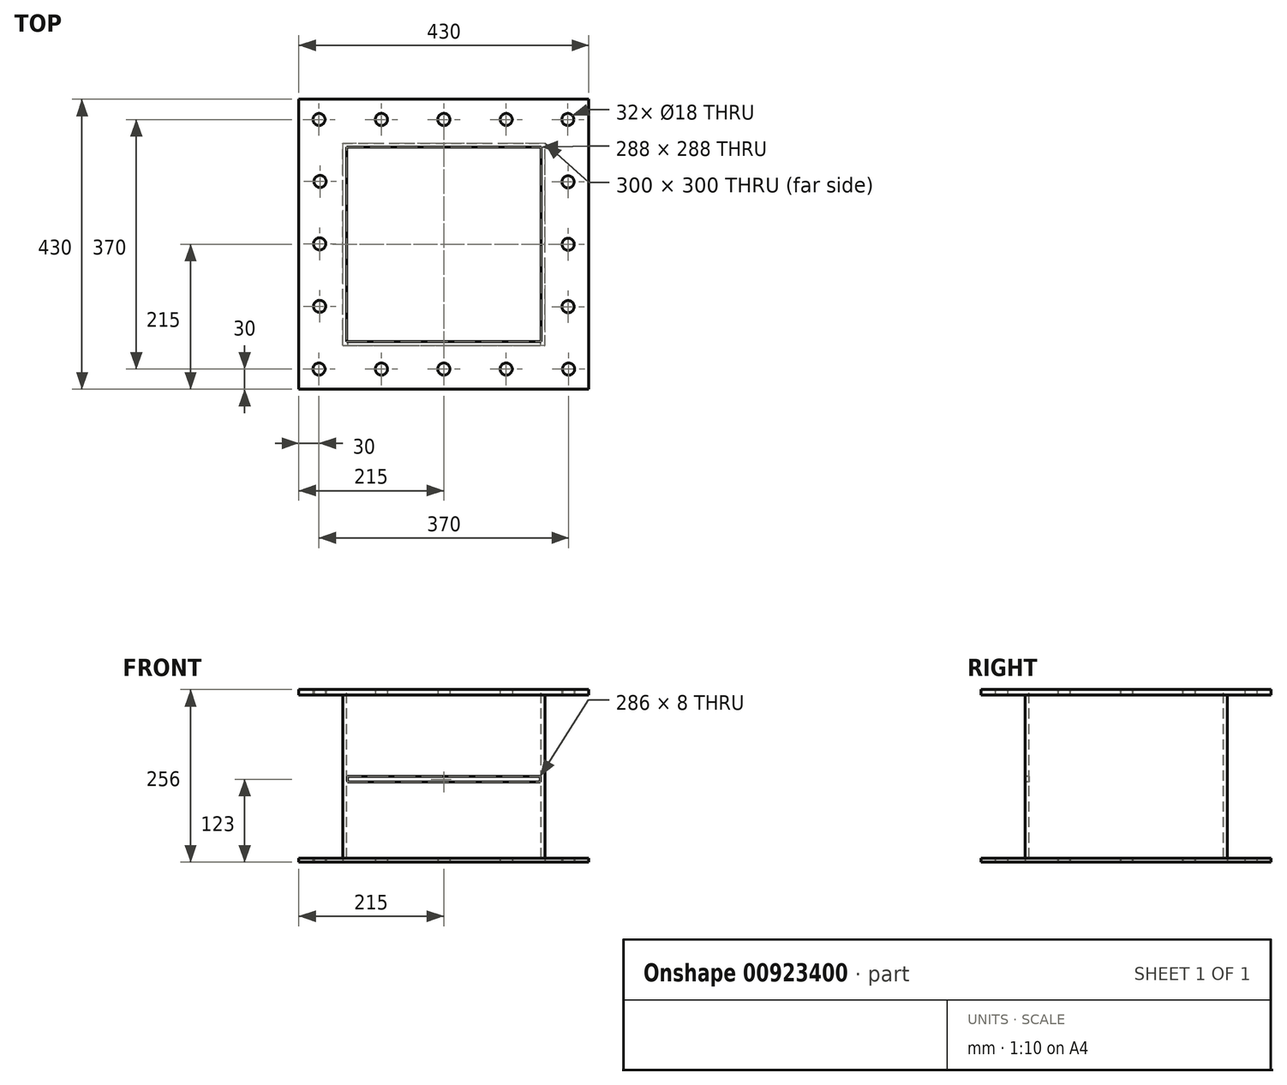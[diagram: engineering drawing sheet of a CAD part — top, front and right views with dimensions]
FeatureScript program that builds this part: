
annotation { "Feature Type Name" : "Feature", "Feature Type Description" : "" }
export const myFeature = defineFeature(function(context is Context, id is Id, definition is map)
    precondition{}
    {
        {
            var Q0;
            Q0=qCreatedBy(makeId("Top.planeOp"),FACE);
            var sketch = newSketch(context, id + "F0", { "sketchPlane" : qUnion([Q0])});
            skLineSegment(sketch, "E0.bottom", {"start": v(-215.44, -118.11) * mm, "end": v(214.56, -118.11) * mm});
            skLineSegment(sketch, "E0.top", {"start": v(-215.44, 311.89) * mm, "end": v(214.56, 311.89) * mm});
            skLineSegment(sketch, "E0.left", {"start": v(-215.44, -118.11) * mm, "end": v(-215.44, 311.89) * mm});
            skLineSegment(sketch, "E0.right", {"start": v(214.56, -118.11) * mm, "end": v(214.56, 311.89) * mm});
            skLineSegment(sketch, "E1.0", {"start": v(-150.44, -53.11) * mm, "end": v(149.56, -53.11) * mm});
            skLineSegment(sketch, "E1.1", {"start": v(-150.44, -53.11) * mm, "end": v(-150.44, 246.89) * mm});
            skLineSegment(sketch, "E1.2", {"start": v(-150.44, 246.89) * mm, "end": v(149.56, 246.89) * mm});
            skLineSegment(sketch, "E1.3", {"start": v(149.56, -53.11) * mm, "end": v(149.56, 246.89) * mm});
            skSolve(sketch);
        }
        {
            var Q0;
            Q0=makeQuery(id+"F0.imprint","IMPRINT",FACE,{"disambiguationData":[TD([[makeQuery(id+"F0.imprint","IMPRINT",EDGE,{"derivedFrom":sQuery(id+"F0.wireOp",EDGE,"E0.bottom")}),1.0]])]});
            extrude(context, id + "F1", {"entities" : qUnion([Q0]), "depth" : 6 * mm, "offsetDistance" : 25.4 * mm});
        }
        {
            var Q0;
            Q0=makeQuery(id+"F1.opExtrude","CAP_FACE",FACE,{"disambiguationData":[OSD([sQuery(id+"F0.wireOp",EDGE,"E0.bottom"),sQuery(id+"F0.wireOp",EDGE,"E0.top"),sQuery(id+"F0.wireOp",EDGE,"E0.left"),sQuery(id+"F0.wireOp",EDGE,"E0.right"),sQuery(id+"F0.wireOp",EDGE,"E1.0"),sQuery(id+"F0.wireOp",EDGE,"E1.1"),sQuery(id+"F0.wireOp",EDGE,"E1.2"),sQuery(id+"F0.wireOp",EDGE,"E1.3")])],"isStart":false});
            var sketch = newSketch(context, id + "F2", { "sketchPlane" : qUnion([Q0])});
            skLineSegment(sketch, "E2.0", {"start": v(-150.44, -53.11) * mm, "end": v(-150.44, 246.89) * mm});
            skLineSegment(sketch, "E3.0", {"start": v(-150.44, 246.89) * mm, "end": v(149.56, 246.89) * mm});
            skLineSegment(sketch, "E4.0", {"start": v(149.56, -53.11) * mm, "end": v(149.56, 246.89) * mm});
            skLineSegment(sketch, "E5.0", {"start": v(-150.44, -53.11) * mm, "end": v(149.56, -53.11) * mm});
            skSolve(sketch);
        }
        {
            var Q0;
            Q0=makeQuery(id+"F2.imprint","IMPRINT",FACE,{"disambiguationData":[TD([[makeQuery(id+"F2.imprint","IMPRINT",EDGE,{"derivedFrom":sQuery(id+"F2.wireOp",EDGE,"E5.0")}),1.0]])]});
            extrude(context, id + "F3", {"entities" : qUnion([Q0]), "depth" : 250 * mm, "offsetDistance" : 25.4 * mm});
        }
        {
            var Q0;
            Q0=makeQuery(id+"F3.opExtrude","CAP_FACE",FACE,{"disambiguationData":[OSD([sQuery(id+"F2.wireOp",EDGE,"E5.0"),sQuery(id+"F2.wireOp",EDGE,"E3.0"),sQuery(id+"F2.wireOp",EDGE,"E2.0"),sQuery(id+"F2.wireOp",EDGE,"E4.0")])],"isStart":false});
            var sketch = newSketch(context, id + "F4", { "sketchPlane" : qUnion([Q0])});
            skLineSegment(sketch, "E6.0", {"start": v(143.56, -47.11) * mm, "end": v(143.56, 240.89) * mm});
            skLineSegment(sketch, "E6.1", {"start": v(-144.44, -47.11) * mm, "end": v(143.56, -47.11) * mm});
            skLineSegment(sketch, "E6.2", {"start": v(-144.44, -47.11) * mm, "end": v(-144.44, 240.89) * mm});
            skLineSegment(sketch, "E6.3", {"start": v(-144.44, 240.89) * mm, "end": v(143.56, 240.89) * mm});
            skSolve(sketch);
        }
        {
            var Q0;
            Q0=makeQuery(id+"F4.imprint","IMPRINT",FACE,{"disambiguationData":[TD([[makeQuery(id+"F4.imprint","IMPRINT",EDGE,{"derivedFrom":sQuery(id+"F4.wireOp",EDGE,"E6.0")}),1.0]])]});
            extrude(context, id + "F5", {"entities" : qUnion([Q0]), "operationType" : NewBodyOperationType.REMOVE, "oppositeDirection" : true, "depth" : 566.42 * mm, "offsetDistance" : 25.4 * mm});
        }
        {
            var Q0;
            Q0=makeQuery(id+"F3.opExtrude","CAP_FACE",FACE,{"disambiguationData":[OSD([sQuery(id+"F2.wireOp",EDGE,"E5.0"),sQuery(id+"F2.wireOp",EDGE,"E3.0"),sQuery(id+"F2.wireOp",EDGE,"E2.0"),sQuery(id+"F2.wireOp",EDGE,"E4.0")])],"isStart":false});
            var sketch = newSketch(context, id + "F6", { "sketchPlane" : qUnion([Q0])});
            skLineSegment(sketch, "E7.bottom", {"start": v(-150.44, 246.89) * mm, "end": v(149.56, 246.89) * mm});
            skLineSegment(sketch, "E7.top", {"start": v(-150.44, -53.11) * mm, "end": v(149.56, -53.11) * mm});
            skLineSegment(sketch, "E7.left", {"start": v(-150.44, 246.89) * mm, "end": v(-150.44, -53.11) * mm});
            skLineSegment(sketch, "E7.right", {"start": v(149.56, 246.89) * mm, "end": v(149.56, -53.11) * mm});
            skLineSegment(sketch, "E8.0", {"start": v(214.56, 311.89) * mm, "end": v(214.56, -118.11) * mm});
            skLineSegment(sketch, "E8.1", {"start": v(-215.44, 311.89) * mm, "end": v(214.56, 311.89) * mm});
            skLineSegment(sketch, "E8.2", {"start": v(-215.44, 311.89) * mm, "end": v(-215.44, -118.11) * mm});
            skLineSegment(sketch, "E8.3", {"start": v(-215.44, -118.11) * mm, "end": v(214.56, -118.11) * mm});
            skSolve(sketch);
        }
        {
            var Q0;
            Q0=makeQuery(id+"F6.imprint","IMPRINT",FACE,{"disambiguationData":[TD([[makeQuery(id+"F6.imprint","IMPRINT",EDGE,{"derivedFrom":sQuery(id+"F6.wireOp",EDGE,"E7.bottom")}),1.0]])]});
            extrude(context, id + "F7", {"entities" : qUnion([Q0]), "operationType" : NewBodyOperationType.ADD, "oppositeDirection" : true, "depth" : 8 * mm, "offsetDistance" : 25.4 * mm});
        }
        {
            var Q0;
            Q0=makeQuery(id+"F3.opExtrude","SWEPT_FACE",FACE,{"disambiguationData":[OSD([sQuery(id+"F2.wireOp",EDGE,"E5.0")])]});
            var sketch = newSketch(context, id + "F8", { "sketchPlane" : qUnion([Q0])});
            skLineSegment(sketch, "E9.0", {"start": v(-143.44, 127) * mm, "end": v(-143.44, 119) * mm});
            skLineSegment(sketch, "E10.0", {"start": v(142.56, 127) * mm, "end": v(142.56, 119) * mm});
            skLineSegment(sketch, "E11", {"start": v(-143.44, 127) * mm, "end": v(142.56, 127) * mm});
            skLineSegment(sketch, "E12.0", {"start": v(-143.44, 119) * mm, "end": v(142.56, 119) * mm});
            skPoint(sketch, "E13.orphan", {"position": v(-143.44, 248) * mm});
            skPoint(sketch, "E14.orphan", {"position": v(-143.44, 6) * mm});
            skPoint(sketch, "E15.orphan", {"position": v(142.56, 6) * mm});
            skPoint(sketch, "E16.orphan", {"position": v(142.56, 248) * mm});
            skSolve(sketch);
        }
        {
            var Q0;
            Q0=makeQuery(id+"F8.imprint","IMPRINT",FACE,{"disambiguationData":[TD([[makeQuery(id+"F8.imprint","IMPRINT",EDGE,{"derivedFrom":sQuery(id+"F8.wireOp",EDGE,"E9.0")}),1.0]])]});
            var Q1;
            Q1=makeQuery(id+"F5.boolean.opBoolean","COPY",FACE,{"derivedFrom":makeQuery(id+"F5.opExtrude","SWEPT_FACE",FACE,{"disambiguationData":[OSD([sQuery(id+"F4.wireOp",EDGE,"E6.3")])]})});
            extrude(context, id + "F9", {"entities" : qUnion([Q0]), "operationType" : NewBodyOperationType.REMOVE, "endBound" : BoundingType.UP_TO_SURFACE, "oppositeDirection" : true, "depth" : 279.4 * mm, "endBoundEntityFace" : qUnion([Q1]), "offsetDistance" : 25.4 * mm});
        }
        {
            var Q0;
            Q0=makeQuery(id+"F7.boolean.opBoolean","MERGE",FACE,{"derivedFrom":[makeQuery(id+"F3.opExtrude","CAP_FACE",FACE,{"disambiguationData":[OSD([sQuery(id+"F2.wireOp",EDGE,"E5.0"),sQuery(id+"F2.wireOp",EDGE,"E3.0"),sQuery(id+"F2.wireOp",EDGE,"E2.0"),sQuery(id+"F2.wireOp",EDGE,"E4.0")])],"isStart":false}),makeQuery(id+"F7.opExtrude","CAP_FACE",FACE,{"disambiguationData":[OSD([sQuery(id+"F6.wireOp",EDGE,"E7.bottom"),sQuery(id+"F6.wireOp",EDGE,"E7.top"),sQuery(id+"F6.wireOp",EDGE,"E7.left"),sQuery(id+"F6.wireOp",EDGE,"E7.right"),sQuery(id+"F6.wireOp",EDGE,"E8.0"),sQuery(id+"F6.wireOp",EDGE,"E8.1"),sQuery(id+"F6.wireOp",EDGE,"E8.2"),sQuery(id+"F6.wireOp",EDGE,"E8.3")])],"isStart":true})]});
            var sketch = newSketch(context, id + "F10", { "sketchPlane" : qUnion([Q0])});
            skCircle(sketch, "E17", {"center": v(184.56, -88.11) * mm, "radius": 9 * mm});
            skCircle(sketch, "E18.1.0.0", {"center": v(92.06, -88.11) * mm, "radius": 9 * mm});
            skCircle(sketch, "E18.2.0.0", {"center": v(-0.44, -88.11) * mm, "radius": 9 * mm});
            skCircle(sketch, "E18.3.0.0", {"center": v(-92.94, -88.11) * mm, "radius": 9 * mm});
            skCircle(sketch, "E18.4.0.0", {"center": v(-185.44, -88.11) * mm, "radius": 9 * mm});
            skLineSegment(sketch, "E18.direction1", {"start": v(184.56, -88.11) * mm, "end": v(92.06, -88.11) * mm, "construction": true});
            skCircle(sketch, "E19.MirrorC", {"center": v(-185.44, 281.89) * mm, "radius": 9 * mm});
            skCircle(sketch, "E20.MirrorC", {"center": v(-92.94, 281.89) * mm, "radius": 9 * mm});
            skCircle(sketch, "E21.MirrorC", {"center": v(-0.44, 281.89) * mm, "radius": 9 * mm});
            skCircle(sketch, "E22.MirrorC", {"center": v(92.06, 281.89) * mm, "radius": 9 * mm});
            skCircle(sketch, "E23.MirrorC", {"center": v(183.48, 281.89) * mm, "radius": 9 * mm});
            skLineSegment(sketch, "E24", {"start": v(184.56, -88.11) * mm, "end": v(184.54, -79.11) * mm});
            skCircle(sketch, "E25", {"center": v(184.02, 96.89) * mm, "radius": 9 * mm});
            skCircle(sketch, "E26", {"center": v(183.75, 189.39) * mm, "radius": 9 * mm});
            skCircle(sketch, "E27.MirrorC", {"center": v(183.75, 4.4) * mm, "radius": 9 * mm});
            skCircle(sketch, "E28.MirrorC", {"center": v(-184.47, 4.95) * mm, "radius": 9 * mm});
            skCircle(sketch, "E29.MirrorC", {"center": v(-183.9, 189.95) * mm, "radius": 9 * mm});
            skCircle(sketch, "E30.MirrorC", {"center": v(-184.46, 97.45) * mm, "radius": 9 * mm});
            skSolve(sketch);
        }
        {
            var Q0;
            Q0=sQuery(id+"F10.wireOp",VERTEX,"E18.4.0.0.center");
            var Q1;
            Q1=sQuery(id+"F10.wireOp",VERTEX,"E28.MirrorC.center");
            var Q2;
            Q2=sQuery(id+"F10.wireOp",VERTEX,"E30.MirrorC.center");
            var Q3;
            Q3=sQuery(id+"F10.wireOp",VERTEX,"E29.MirrorC.center");
            var Q4;
            Q4=sQuery(id+"F10.wireOp",VERTEX,"E19.MirrorC.center");
            var Q5;
            Q5=sQuery(id+"F10.wireOp",VERTEX,"E20.MirrorC.center");
            var Q6;
            Q6=sQuery(id+"F10.wireOp",VERTEX,"E21.MirrorC.center");
            var Q7;
            Q7=sQuery(id+"F10.wireOp",VERTEX,"E22.MirrorC.center");
            var Q8;
            Q8=sQuery(id+"F10.wireOp",VERTEX,"E23.MirrorC.center");
            var Q9;
            Q9=sQuery(id+"F10.wireOp",VERTEX,"E26.center");
            var Q10;
            Q10=sQuery(id+"F10.wireOp",VERTEX,"E25.center");
            var Q11;
            Q11=sQuery(id+"F10.wireOp",VERTEX,"E27.MirrorC.center");
            var Q12;
            Q12=sQuery(id+"F10.wireOp",VERTEX,"E18.direction1.start");
            var Q13;
            Q13=sQuery(id+"F10.wireOp",VERTEX,"E18.direction1.end");
            var Q14;
            Q14=sQuery(id+"F10.wireOp",VERTEX,"E18.2.0.0.center");
            var Q15;
            Q15=sQuery(id+"F10.wireOp",VERTEX,"E18.3.0.0.center");
            var Q16;
            Q16=makeQuery(id+"F3.opExtrude","SWEPT_BODY",BODY,{"disambiguationData":[OSD([sQuery(id+"F2.wireOp",EDGE,"E5.0"),sQuery(id+"F2.wireOp",EDGE,"E3.0"),sQuery(id+"F2.wireOp",EDGE,"E2.0"),sQuery(id+"F2.wireOp",EDGE,"E4.0")])]});
            var Q17;
            Q17=makeQuery(id+"F1.opExtrude","SWEPT_BODY",BODY,{"disambiguationData":[OSD([sQuery(id+"F0.wireOp",EDGE,"E0.bottom"),sQuery(id+"F0.wireOp",EDGE,"E0.top"),sQuery(id+"F0.wireOp",EDGE,"E0.left"),sQuery(id+"F0.wireOp",EDGE,"E0.right"),sQuery(id+"F0.wireOp",EDGE,"E1.0"),sQuery(id+"F0.wireOp",EDGE,"E1.1"),sQuery(id+"F0.wireOp",EDGE,"E1.2"),sQuery(id+"F0.wireOp",EDGE,"E1.3")])]});
            hole(context, id + "F11", {"style" : HoleStyle.SIMPLE, "endStyle" : HoleEndStyle.THROUGH, "holeDiameter" : 18 * mm, "majorDiameter" : 6.35 * mm, "isTappedThrough" : true, "tappedDepth" : 12.7 * mm, "tapClearance" : 3, "startFromSketch" : true, "locations" : qUnion([Q0, Q1, Q2, Q3, Q4, Q5, Q6, Q7, Q8, Q9, Q10, Q11, Q12, Q13, Q14, Q15]), "scope" : qUnion([Q16, Q17])});
        }
    });
